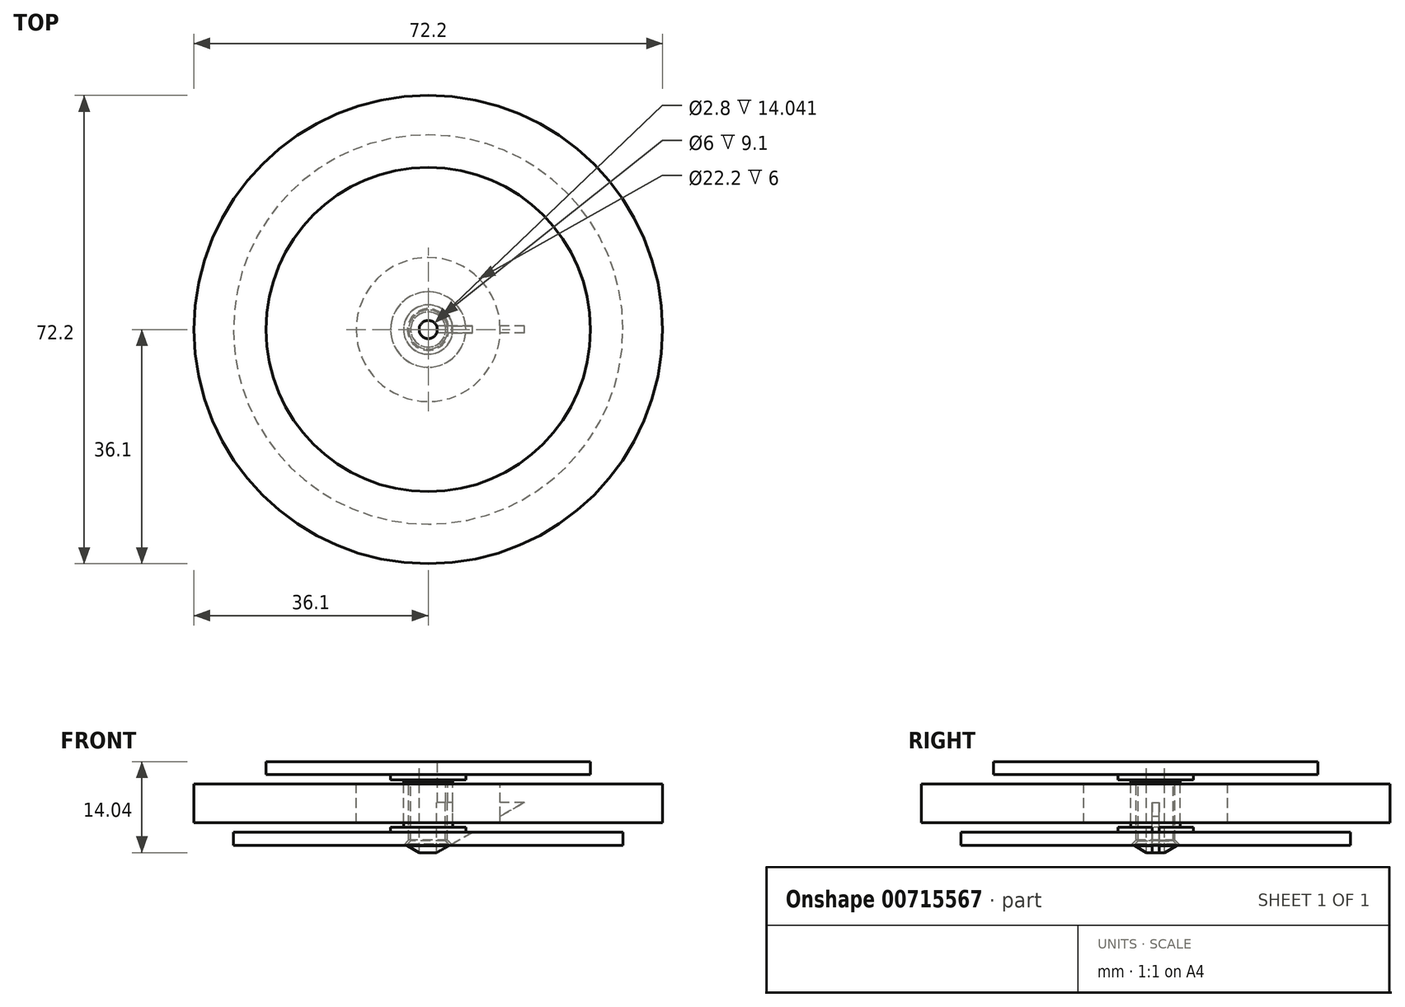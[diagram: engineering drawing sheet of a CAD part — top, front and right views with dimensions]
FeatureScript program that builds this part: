
annotation { "Feature Type Name" : "Feature", "Feature Type Description" : "" }
export const myFeature = defineFeature(function(context is Context, id is Id, definition is map)
    precondition{}
    {
        {
            var Q0;
            Q0=qCreatedBy(makeId("Front.planeOp"),FACE);
            var sketch = newSketch(context, id + "F0", { "sketchPlane" : qUnion([Q0])});
            skLineSegment(sketch, "E0", {"start": v(0, 86.94) * mm, "end": v(0, -87.04) * mm, "construction": true});
            skLineSegment(sketch, "E1", {"start": v(-1.4, 0) * mm, "end": v(-25, 0) * mm});
            skLineSegment(sketch, "E2", {"start": v(-25, 0) * mm, "end": v(-25, -2) * mm});
            skLineSegment(sketch, "E3", {"start": v(-2.7, -2.8) * mm, "end": v(-2.7, -12.22) * mm});
            skLineSegment(sketch, "E4", {"start": v(-2.7, -12.22) * mm, "end": v(-3.2, -12.72) * mm});
            skLineSegment(sketch, "E5", {"start": v(-3.2, -12.9) * mm, "end": v(-1.4, -12.9) * mm, "construction": true});
            skLineSegment(sketch, "E6", {"start": v(-1.4, 0) * mm, "end": v(-1.4, -12.9) * mm});
            skLineSegment(sketch, "E7", {"start": v(-3, -12.1) * mm, "end": v(-3.8, -12.9) * mm});
            skLineSegment(sketch, "E8", {"start": v(-3.8, -12.9) * mm, "end": v(-30, -12.9) * mm});
            skLineSegment(sketch, "E9", {"start": v(-3.8, -10.1) * mm, "end": v(-3.8, -3) * mm});
            skLineSegment(sketch, "E10", {"start": v(-3.8, -3) * mm, "end": v(-3, -3) * mm});
            skLineSegment(sketch, "E11", {"start": v(-3, -3) * mm, "end": v(-3, -12.1) * mm});
            skLineSegment(sketch, "E12", {"start": v(-30, -12.9) * mm, "end": v(-30, -10.9) * mm});
            skLineSegment(sketch, "E13", {"start": v(-30, -10.9) * mm, "end": v(-5.8, -10.9) * mm});
            skLineSegment(sketch, "E14", {"start": v(-5.8, -10.9) * mm, "end": v(-5.8, -10.1) * mm});
            skLineSegment(sketch, "E15", {"start": v(-5.8, -10.1) * mm, "end": v(-3.8, -10.1) * mm});
            skLineSegment(sketch, "E16", {"start": v(-2.7, -2.8) * mm, "end": v(-5.8, -2.8) * mm});
            skLineSegment(sketch, "E17", {"start": v(-5.8, -2.8) * mm, "end": v(-5.8, -2) * mm});
            skLineSegment(sketch, "E18", {"start": v(-5.8, -2) * mm, "end": v(-25, -2) * mm});
            skLineSegment(sketch, "E19.bottom", {"start": v(-36.1, -9.45) * mm, "end": v(-11.1, -9.45) * mm});
            skLineSegment(sketch, "E19.top", {"start": v(-36.1, -3.45) * mm, "end": v(-11.1, -3.45) * mm});
            skLineSegment(sketch, "E19.left", {"start": v(-36.1, -9.45) * mm, "end": v(-36.1, -3.45) * mm});
            skLineSegment(sketch, "E19.right", {"start": v(-11.1, -9.45) * mm, "end": v(-11.1, -3.45) * mm});
            skPoint(sketch, "E19.middle", {"position": v(-23.6, -6.45) * mm});
            skLineSegment(sketch, "E20", {"start": v(-3.2, -13) * mm, "end": v(-1.4, -14.04) * mm});
            skLineSegment(sketch, "E21", {"start": v(-1.4, -14.04) * mm, "end": v(-1.4, -12.9) * mm});
            skLineSegment(sketch, "E22", {"start": v(-3.2, -13) * mm, "end": v(-3.2, -12.72) * mm});
            skPoint(sketch, "E23.orphan", {"position": v(-3.38, -12.9) * mm});
            skLineSegment(sketch, "E24", {"start": v(-23.6, -6.45) * mm, "end": v(-23.6, -12.9) * mm, "construction": true});
            skLineSegment(sketch, "E25", {"start": v(-23.6, -6.45) * mm, "end": v(-23.6, 0) * mm, "construction": true});
            skSolve(sketch);
        }
        {
            var Q0;
            Q0 = qSketchRegion(id + "F0", true);
            var Q1;
            Q1=sQuery(id+"F0.wireOp",EDGE,"E0");
            revolve(context, id + "F1", {"surfaceOperationType" : NewSurfaceOperationType.NEW, "entities" : qUnion([Q0]), "axis" : qUnion([Q1]), "revolveType" : RevolveType.FULL});
        }
        {
            var Q0;
            Q0=qCreatedBy(makeId("Right.planeOp"),FACE);
            var sketch = newSketch(context, id + "F2", { "sketchPlane" : qUnion([Q0])});
            skLineSegment(sketch, "E26.0", {"start": v(-5.8, -2.8) * mm, "end": v(5.8, -2.8) * mm, "construction": true});
            skLineSegment(sketch, "E27.bottom", {"start": v(-0.55, -6.3) * mm, "end": v(0.55, -6.3) * mm});
            skLineSegment(sketch, "E27.top", {"start": v(-0.55, -14.04) * mm, "end": v(0.55, -14.04) * mm});
            skLineSegment(sketch, "E27.left", {"start": v(-0.55, -6.3) * mm, "end": v(-0.55, -14.04) * mm});
            skLineSegment(sketch, "E27.right", {"start": v(0.55, -6.3) * mm, "end": v(0.55, -14.04) * mm});
            skPoint(sketch, "E27.middle", {"position": v(0, -10.17) * mm});
            skLineSegment(sketch, "E28.0", {"start": v(-1.4, -14.04) * mm, "end": v(1.4, -14.04) * mm, "construction": true});
            skSolve(sketch);
        }
        {
            var Q0;
            Q0=makeQuery(id+"F2.imprint","IMPRINT",FACE,{"disambiguationData":[TD([[makeQuery(id+"F2.imprint","IMPRINT",EDGE,{"derivedFrom":sQuery(id+"F2.wireOp",EDGE,"E27.bottom")}),-1.0]])]});
            var Q1;
            Q1=makeQuery(id+"F1.opRevolve","SWEPT_FACE",FACE,{"disambiguationData":[OSD([sQuery(id+"F0.wireOp",EDGE,"E20")])]});
            extrude(context, id + "F3", {"entities" : qUnion([Q0]), "operationType" : NewBodyOperationType.REMOVE, "endBound" : BoundingType.UP_TO_SURFACE, "depth" : 25 * mm, "endBoundEntityFace" : qUnion([Q1]), "offsetDistance" : 25 * mm});
        }
    });
